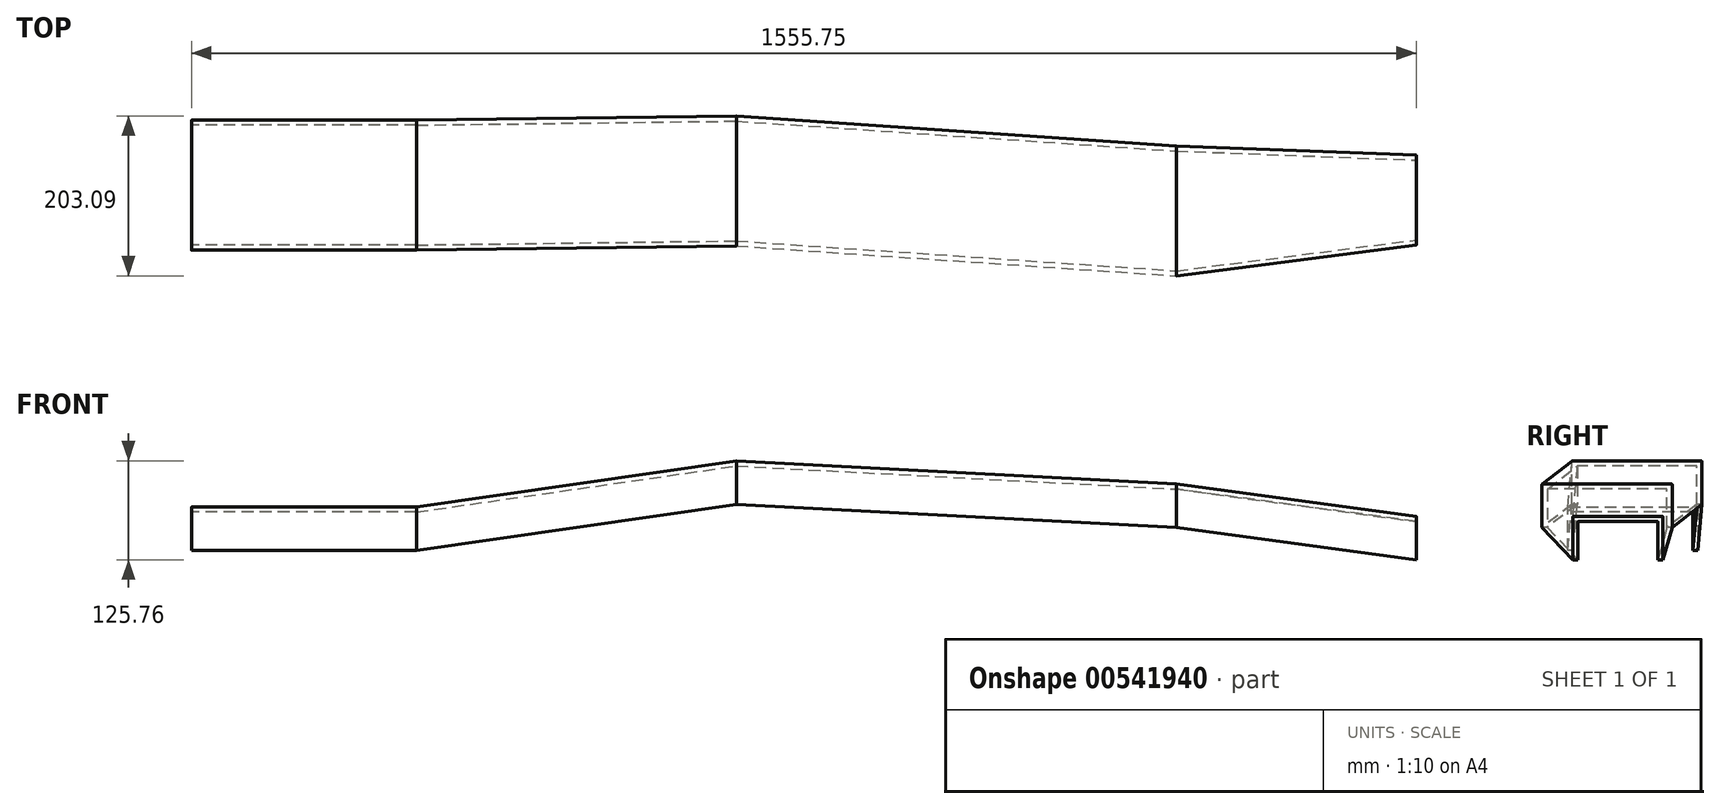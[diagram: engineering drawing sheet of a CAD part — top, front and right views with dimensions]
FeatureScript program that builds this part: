
annotation { "Feature Type Name" : "Feature", "Feature Type Description" : "" }
export const myFeature = defineFeature(function(context is Context, id is Id, definition is map)
    precondition{}
    {
        {
            var Q0;
            Q0=qCreatedBy(makeId("Right.planeOp"),FACE);
            var sketch = newSketch(context, id + "F0", { "sketchPlane" : qUnion([Q0])});
            skLineSegment(sketch, "E0", {"start": v(139.2, -0.63) * mm, "end": v(139.2, -55.25) * mm});
            skLineSegment(sketch, "E1", {"start": v(139.2, -55.25) * mm, "end": v(132.76, -55.25) * mm});
            skLineSegment(sketch, "E2", {"start": v(132.76, -55.25) * mm, "end": v(132.76, -7.07) * mm});
            skLineSegment(sketch, "E3", {"start": v(132.13, -6.43) * mm, "end": v(-18.84, -6.43) * mm});
            skLineSegment(sketch, "E4", {"start": v(-19.47, -7.07) * mm, "end": v(-19.47, -55.25) * mm});
            skLineSegment(sketch, "E5", {"start": v(-19.47, -55.25) * mm, "end": v(-25.9, -55.25) * mm});
            skLineSegment(sketch, "E6", {"start": v(-25.9, -55.25) * mm, "end": v(-25.9, -0.64) * mm});
            skLineSegment(sketch, "E7", {"start": v(-25.27, 0) * mm, "end": v(138.56, 0) * mm});
            skPoint(sketch, "E8.visualSharp", {"position": v(132.76, -6.43) * mm});
            skArc(sketch, "E8.filletArc", {"start": v(132.76, -7.07) * mm, "mid": v(132.57, -6.62) * mm, "end": v(132.13, -6.43) * mm});
            skPoint(sketch, "E9.visualSharp", {"position": v(-19.47, -6.43) * mm});
            skArc(sketch, "E9.filletArc", {"start": v(-18.84, -6.43) * mm, "mid": v(-19.29, -6.62) * mm, "end": v(-19.47, -7.07) * mm});
            skPoint(sketch, "E10.visualSharp", {"position": v(139.2, 0) * mm});
            skArc(sketch, "E10.filletArc", {"start": v(139.2, -0.63) * mm, "mid": v(139, -0.19) * mm, "end": v(138.56, 0) * mm});
            skPoint(sketch, "E11.visualSharp", {"position": v(-25.9, 0) * mm});
            skArc(sketch, "E11.filletArc", {"start": v(-25.27, 0) * mm, "mid": v(-25.72, -0.19) * mm, "end": v(-25.9, -0.64) * mm});
            skSolve(sketch);
        }
        {
            var Q0;
            Q0 = qSketchRegion(id + "F0", true);
            extrude(context, id + "F1", {"entities" : qUnion([Q0]), "depth" : 285.75 * mm, "offsetDistance" : 25.4 * mm});
        }
        {
            var Q0;
            Q0=makeQuery(id+"F1.opExtrude","CAP_FACE",FACE,{"disambiguationData":[OSD([sQuery(id+"F0.wireOp",EDGE,"E0"),sQuery(id+"F0.wireOp",EDGE,"E1"),sQuery(id+"F0.wireOp",EDGE,"E2"),sQuery(id+"F0.wireOp",EDGE,"E3"),sQuery(id+"F0.wireOp",EDGE,"E4"),sQuery(id+"F0.wireOp",EDGE,"E5"),sQuery(id+"F0.wireOp",EDGE,"E6"),sQuery(id+"F0.wireOp",EDGE,"E7"),sQuery(id+"F0.wireOp",EDGE,"E8.filletArc"),sQuery(id+"F0.wireOp",EDGE,"E9.filletArc"),sQuery(id+"F0.wireOp",EDGE,"E10.filletArc"),sQuery(id+"F0.wireOp",EDGE,"E11.filletArc")])],"isStart":false});
            cPlane(context, id + "F2", {"entities" : qUnion([Q0]), "cplaneType" : CPlaneType.OFFSET, "offset" : 406.4 * mm, "width" : 152.4 * mm, "height" : 152.4 * mm});
        }
        {
            var Q0;
            Q0=qCreatedBy(id+"F2.planeOp",FACE);
            var sketch = newSketch(context, id + "F3", { "sketchPlane" : qUnion([Q0])});
            skLineSegment(sketch, "E12", {"start": v(61.8, -7.3) * mm, "end": v(167.19, -7.3) * mm, "construction": true});
            skLineSegment(sketch, "E13", {"start": v(61.8, -7.3) * mm, "end": v(-84.88, -7.3) * mm, "construction": true});
            skLineSegment(sketch, "E14", {"start": v(61.8, -7.3) * mm, "end": v(61.8, -122.91) * mm, "construction": true});
            skLineSegment(sketch, "E15", {"start": v(61.8, -52.51) * mm, "end": v(61.8, 50.94) * mm, "construction": true});
            skLineSegment(sketch, "E16", {"start": v(144.33, 57.92) * mm, "end": v(144.33, 3.31) * mm});
            skLineSegment(sketch, "E17", {"start": v(144.33, 3.31) * mm, "end": v(137.9, 3.31) * mm});
            skLineSegment(sketch, "E18", {"start": v(137.9, 3.31) * mm, "end": v(137.9, 51.49) * mm});
            skLineSegment(sketch, "E19", {"start": v(137.26, 52.12) * mm, "end": v(-13.7, 52.12) * mm});
            skLineSegment(sketch, "E20", {"start": v(-14.34, 51.49) * mm, "end": v(-14.34, 3.31) * mm});
            skLineSegment(sketch, "E21", {"start": v(-14.34, 3.31) * mm, "end": v(-20.77, 3.31) * mm});
            skLineSegment(sketch, "E22", {"start": v(-20.77, 3.31) * mm, "end": v(-20.77, 57.92) * mm});
            skLineSegment(sketch, "E23", {"start": v(-20.14, 58.56) * mm, "end": v(143.7, 58.56) * mm});
            skPoint(sketch, "E24.visualSharp", {"position": v(137.9, 52.12) * mm});
            skArc(sketch, "E24.filletArc", {"start": v(137.9, 51.49) * mm, "mid": v(137.7, 51.94) * mm, "end": v(137.26, 52.12) * mm});
            skPoint(sketch, "E25.visualSharp", {"position": v(-14.34, 52.12) * mm});
            skArc(sketch, "E25.filletArc", {"start": v(-13.7, 52.12) * mm, "mid": v(-14.16, 51.94) * mm, "end": v(-14.34, 51.49) * mm});
            skPoint(sketch, "E26.visualSharp", {"position": v(144.33, 58.56) * mm});
            skArc(sketch, "E26.filletArc", {"start": v(144.33, 57.92) * mm, "mid": v(144.14, 58.37) * mm, "end": v(143.7, 58.56) * mm});
            skPoint(sketch, "E27.visualSharp", {"position": v(-20.77, 58.56) * mm});
            skArc(sketch, "E27.filletArc", {"start": v(-20.14, 58.56) * mm, "mid": v(-20.59, 58.37) * mm, "end": v(-20.77, 57.92) * mm});
            skSolve(sketch);
        }
        {
            var Q1;
            Q1=makeQuery(id+"F1.opExtrude","CAP_FACE",FACE,{"disambiguationData":[OSD([sQuery(id+"F0.wireOp",EDGE,"E0"),sQuery(id+"F0.wireOp",EDGE,"E1"),sQuery(id+"F0.wireOp",EDGE,"E2"),sQuery(id+"F0.wireOp",EDGE,"E3"),sQuery(id+"F0.wireOp",EDGE,"E4"),sQuery(id+"F0.wireOp",EDGE,"E5"),sQuery(id+"F0.wireOp",EDGE,"E6"),sQuery(id+"F0.wireOp",EDGE,"E7"),sQuery(id+"F0.wireOp",EDGE,"E8.filletArc"),sQuery(id+"F0.wireOp",EDGE,"E9.filletArc"),sQuery(id+"F0.wireOp",EDGE,"E10.filletArc"),sQuery(id+"F0.wireOp",EDGE,"E11.filletArc")])],"isStart":false});
            var Q2;
            Q2=makeQuery(id+"F3.imprint","IMPRINT",FACE,{"disambiguationData":[TD([[makeQuery(id+"F3.imprint","IMPRINT",EDGE,{"derivedFrom":sQuery(id+"F3.wireOp",EDGE,"E16")}),-1.0]])]});
            loft(context, id + "F4", {"operationType" : NewBodyOperationType.ADD, "sheetProfilesArray" : [{ "sheetProfileEntities" : qUnion([Q1]) }, { "sheetProfileEntities" : qUnion([Q2]) }]});
        }
        {
            var Q0;
            Q0=qCreatedBy(id+"F2.planeOp",FACE);
            cPlane(context, id + "F5", {"entities" : qUnion([Q0]), "cplaneType" : CPlaneType.OFFSET, "offset" : 558.8 * mm, "width" : 152.4 * mm, "height" : 152.4 * mm});
        }
        {
            var Q0;
            Q0=qCreatedBy(id+"F5.planeOp",FACE);
            var sketch = newSketch(context, id + "F6", { "sketchPlane" : qUnion([Q0])});
            skLineSegment(sketch, "E28", {"start": v(61.8, -26.1) * mm, "end": v(167.19, -26.1) * mm, "construction": true});
            skLineSegment(sketch, "E29", {"start": v(61.8, -26.1) * mm, "end": v(-58.76, -26.1) * mm, "construction": true});
            skLineSegment(sketch, "E30", {"start": v(61.8, -26.1) * mm, "end": v(61.8, -141.72) * mm, "construction": true});
            skLineSegment(sketch, "E31", {"start": v(61.8, -26.1) * mm, "end": v(61.8, 77.35) * mm, "construction": true});
            skLineSegment(sketch, "E32", {"start": v(-37.33, -26.1) * mm, "end": v(61.8, 77.35) * mm, "construction": true});
            skLineSegment(sketch, "E33", {"start": v(-37.33, 77.35) * mm, "end": v(61.8, 77.35) * mm, "construction": true});
            skLineSegment(sketch, "E34", {"start": v(-37.33, -26.1) * mm, "end": v(-37.33, 77.35) * mm, "construction": true});
            skLineSegment(sketch, "E35", {"start": v(106.34, 28.5) * mm, "end": v(106.34, -26.1) * mm});
            skLineSegment(sketch, "E36", {"start": v(106.34, -26.1) * mm, "end": v(99.9, -26.1) * mm});
            skLineSegment(sketch, "E37", {"start": v(99.9, -26.1) * mm, "end": v(99.9, 22.07) * mm});
            skLineSegment(sketch, "E38", {"start": v(99.27, 22.7) * mm, "end": v(-51.69, 22.7) * mm});
            skLineSegment(sketch, "E39", {"start": v(-52.32, 22.07) * mm, "end": v(-52.32, -26.1) * mm});
            skLineSegment(sketch, "E40", {"start": v(-52.32, -26.1) * mm, "end": v(-58.76, -26.1) * mm});
            skLineSegment(sketch, "E41", {"start": v(-58.76, -26.1) * mm, "end": v(-58.76, 28.5) * mm});
            skLineSegment(sketch, "E42", {"start": v(-58.12, 29.14) * mm, "end": v(105.7, 29.14) * mm});
            skPoint(sketch, "E43.visualSharp", {"position": v(99.9, 22.7) * mm});
            skArc(sketch, "E43.filletArc", {"start": v(99.9, 22.07) * mm, "mid": v(99.72, 22.52) * mm, "end": v(99.27, 22.7) * mm});
            skPoint(sketch, "E44.visualSharp", {"position": v(-52.32, 22.7) * mm});
            skArc(sketch, "E44.filletArc", {"start": v(-51.69, 22.7) * mm, "mid": v(-52.14, 22.52) * mm, "end": v(-52.32, 22.07) * mm});
            skPoint(sketch, "E45.visualSharp", {"position": v(106.34, 29.14) * mm});
            skArc(sketch, "E45.filletArc", {"start": v(106.34, 28.5) * mm, "mid": v(106.16, 28.96) * mm, "end": v(105.7, 29.14) * mm});
            skPoint(sketch, "E46.visualSharp", {"position": v(-58.76, 29.14) * mm});
            skArc(sketch, "E46.filletArc", {"start": v(-58.12, 29.14) * mm, "mid": v(-58.57, 28.96) * mm, "end": v(-58.76, 28.5) * mm});
            skSolve(sketch);
        }
        {
            var Q1;
            Q1=makeQuery(id+"F4.opLoft","CAP_FACE",FACE,{"disambiguationData":[OSD([makeQuery(id+"F3.imprint","IMPRINT",FACE,{"disambiguationData":[TD([[makeQuery(id+"F3.imprint","IMPRINT",EDGE,{"derivedFrom":sQuery(id+"F3.wireOp",EDGE,"E16")}),-1.0]])]})])],"isStart":true});
            var Q2;
            Q2=makeQuery(id+"F6.imprint","IMPRINT",FACE,{"disambiguationData":[TD([[makeQuery(id+"F6.imprint","IMPRINT",EDGE,{"derivedFrom":sQuery(id+"F6.wireOp",EDGE,"E35")}),-1.0]])]});
            loft(context, id + "F7", {"operationType" : NewBodyOperationType.ADD, "sheetProfilesArray" : [{ "sheetProfileEntities" : qUnion([Q1]) }, { "sheetProfileEntities" : qUnion([Q2]) }]});
        }
        {
            var Q0;
            Q0=qCreatedBy(id+"F5.planeOp",FACE);
            cPlane(context, id + "F8", {"entities" : qUnion([Q0]), "cplaneType" : CPlaneType.OFFSET, "offset" : 304.8 * mm, "width" : 152.4 * mm, "height" : 152.4 * mm});
        }
        {
            var Q0;
            Q0=qCreatedBy(id+"F8.planeOp",FACE);
            var sketch = newSketch(context, id + "F9", { "sketchPlane" : qUnion([Q0])});
            skLineSegment(sketch, "E47", {"start": v(50.09, -13.24) * mm, "end": v(50.09, -131.95) * mm, "construction": true});
            skLineSegment(sketch, "E48", {"start": v(94.72, -12.59) * mm, "end": v(94.72, -67.2) * mm});
            skLineSegment(sketch, "E49", {"start": v(94.72, -67.2) * mm, "end": v(88.28, -67.2) * mm});
            skLineSegment(sketch, "E50", {"start": v(88.28, -67.2) * mm, "end": v(88.28, -19.02) * mm});
            skLineSegment(sketch, "E51", {"start": v(87.65, -18.38) * mm, "end": v(-12.51, -18.38) * mm});
            skLineSegment(sketch, "E52", {"start": v(-13.15, -19.02) * mm, "end": v(-13.15, -67.2) * mm});
            skLineSegment(sketch, "E53", {"start": v(-13.15, -67.2) * mm, "end": v(-19.58, -67.2) * mm});
            skLineSegment(sketch, "E54", {"start": v(-19.58, -67.2) * mm, "end": v(-19.58, -12.59) * mm});
            skLineSegment(sketch, "E55", {"start": v(-18.95, -11.95) * mm, "end": v(94.08, -11.95) * mm});
            skPoint(sketch, "E56.visualSharp", {"position": v(88.28, -18.38) * mm});
            skArc(sketch, "E56.filletArc", {"start": v(88.28, -19.02) * mm, "mid": v(88.1, -18.57) * mm, "end": v(87.65, -18.38) * mm});
            skPoint(sketch, "E57.visualSharp", {"position": v(-13.15, -18.38) * mm});
            skArc(sketch, "E57.filletArc", {"start": v(-12.51, -18.38) * mm, "mid": v(-12.96, -18.57) * mm, "end": v(-13.15, -19.02) * mm});
            skPoint(sketch, "E58.visualSharp", {"position": v(94.72, -11.95) * mm});
            skArc(sketch, "E58.filletArc", {"start": v(94.72, -12.59) * mm, "mid": v(94.53, -12.14) * mm, "end": v(94.08, -11.95) * mm});
            skPoint(sketch, "E59.visualSharp", {"position": v(-19.58, -11.95) * mm});
            skArc(sketch, "E59.filletArc", {"start": v(-18.95, -11.95) * mm, "mid": v(-19.4, -12.14) * mm, "end": v(-19.58, -12.59) * mm});
            skSolve(sketch);
        }
        {
            var Q1;
            Q1=makeQuery(id+"F7.opLoft","CAP_FACE",FACE,{"disambiguationData":[OSD([makeQuery(id+"F6.imprint","IMPRINT",FACE,{"disambiguationData":[TD([[makeQuery(id+"F6.imprint","IMPRINT",EDGE,{"derivedFrom":sQuery(id+"F6.wireOp",EDGE,"E35")}),-1.0]])]})])],"isStart":true});
            var Q2;
            Q2=makeQuery(id+"F9.imprint","IMPRINT",FACE,{"disambiguationData":[TD([[makeQuery(id+"F9.imprint","IMPRINT",EDGE,{"derivedFrom":sQuery(id+"F9.wireOp",EDGE,"E48")}),-1.0]])]});
            loft(context, id + "F10", {"operationType" : NewBodyOperationType.ADD, "sheetProfilesArray" : [{ "sheetProfileEntities" : qUnion([Q1]) }, { "sheetProfileEntities" : qUnion([Q2]) }]});
        }
    });
